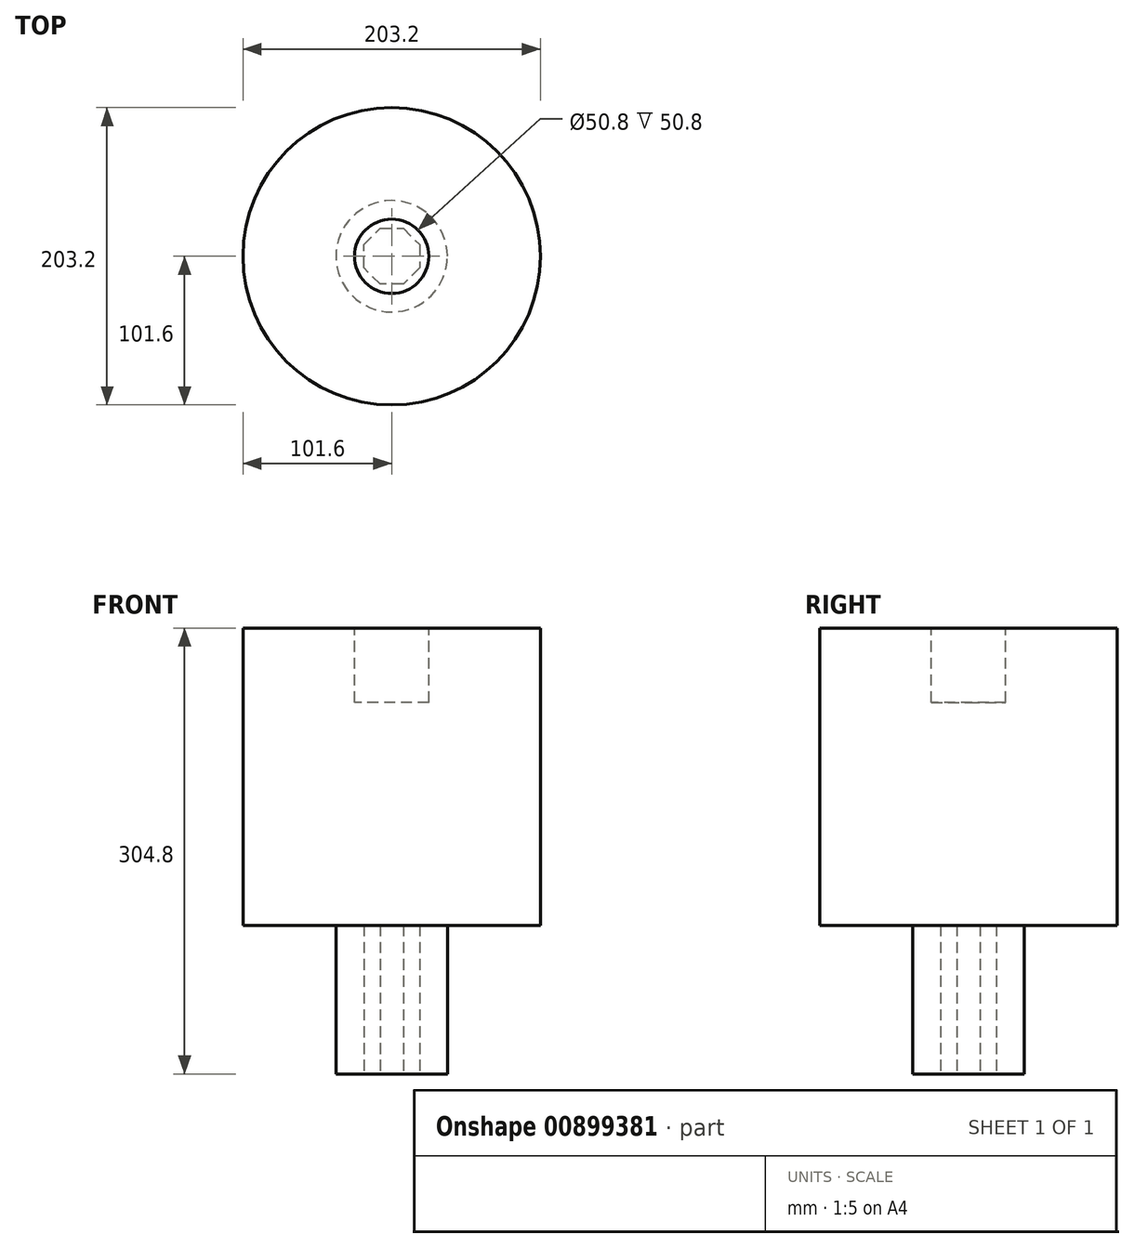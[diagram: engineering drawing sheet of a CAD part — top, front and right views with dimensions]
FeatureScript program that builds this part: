
annotation { "Feature Type Name" : "Feature", "Feature Type Description" : "" }
export const myFeature = defineFeature(function(context is Context, id is Id, definition is map)
    precondition{}
    {
        {
            var Q0;
            Q0=qCreatedBy(makeId("Top.planeOp"),FACE);
            var sketch = newSketch(context, id + "F0", { "sketchPlane" : qUnion([Q0])});
            skCircle(sketch, "E0", {"center": v(0, 0) * mm, "radius": 38.1 * mm});
            skCircle(sketch, "E1.cCircle", {"center": v(0, 0) * mm, "radius": 19.05 * mm, "construction": true});
            skLineSegment(sketch, "E1.0", {"start": v(-7.9, 19.05) * mm, "end": v(7.9, 19.05) * mm});
            skLineSegment(sketch, "E1.1", {"start": v(7.9, 19.05) * mm, "end": v(19.05, 7.9) * mm});
            skLineSegment(sketch, "E1.2", {"start": v(19.05, 7.9) * mm, "end": v(19.05, -7.9) * mm});
            skLineSegment(sketch, "E1.3", {"start": v(19.05, -7.9) * mm, "end": v(7.9, -19.05) * mm});
            skLineSegment(sketch, "E1.4", {"start": v(7.9, -19.05) * mm, "end": v(-7.9, -19.05) * mm});
            skLineSegment(sketch, "E1.5", {"start": v(-7.9, -19.05) * mm, "end": v(-19.05, -7.9) * mm});
            skLineSegment(sketch, "E1.6", {"start": v(-19.05, -7.9) * mm, "end": v(-19.05, 7.9) * mm});
            skLineSegment(sketch, "E1.7", {"start": v(-19.05, 7.9) * mm, "end": v(-7.9, 19.05) * mm});
            skPoint(sketch, "E1.0.midPoint", {"position": v(0, 19.05) * mm});
            skSolve(sketch);
        }
        {
            var Q0;
            Q0 = qSketchRegion(id + "F0", true);
            extrude(context, id + "F1", {"entities" : qUnion([Q0]), "depth" : 101.6 * mm, "offsetDistance" : 25.4 * mm});
        }
        {
            var Q0;
            Q0=makeQuery(id+"F1.opExtrude","CAP_FACE",FACE,{"disambiguationData":[OSD([sQuery(id+"F0.wireOp",EDGE,"E0"),sQuery(id+"F0.wireOp",EDGE,"E1.0"),sQuery(id+"F0.wireOp",EDGE,"E1.1"),sQuery(id+"F0.wireOp",EDGE,"E1.2"),sQuery(id+"F0.wireOp",EDGE,"E1.3"),sQuery(id+"F0.wireOp",EDGE,"E1.4"),sQuery(id+"F0.wireOp",EDGE,"E1.5"),sQuery(id+"F0.wireOp",EDGE,"E1.6"),sQuery(id+"F0.wireOp",EDGE,"E1.7")])],"isStart":false});
            var sketch = newSketch(context, id + "F2", { "sketchPlane" : qUnion([Q0])});
            skCircle(sketch, "E2", {"center": v(0, 0) * mm, "radius": 101.6 * mm});
            skSolve(sketch);
        }
        {
            var Q0;
            Q0 = qSketchRegion(id + "F2", true);
            extrude(context, id + "F3", {"entities" : qUnion([Q0]), "operationType" : NewBodyOperationType.ADD, "depth" : 203.2 * mm, "offsetDistance" : 25.4 * mm});
        }
        {
            var Q0;
            Q0=makeQuery(id+"F3.opExtrude","CAP_FACE",FACE,{"disambiguationData":[OSD([sQuery(id+"F2.wireOp",EDGE,"E2")])],"isStart":false});
            var sketch = newSketch(context, id + "F4", { "sketchPlane" : qUnion([Q0])});
            skCircle(sketch, "E3", {"center": v(0, 0) * mm, "radius": 25.4 * mm});
            skSolve(sketch);
        }
        {
            var Q0;
            Q0 = qSketchRegion(id + "F4", true);
            extrude(context, id + "F5", {"entities" : qUnion([Q0]), "operationType" : NewBodyOperationType.REMOVE, "oppositeDirection" : true, "depth" : 50.8 * mm, "offsetDistance" : 25.4 * mm});
        }
    });
